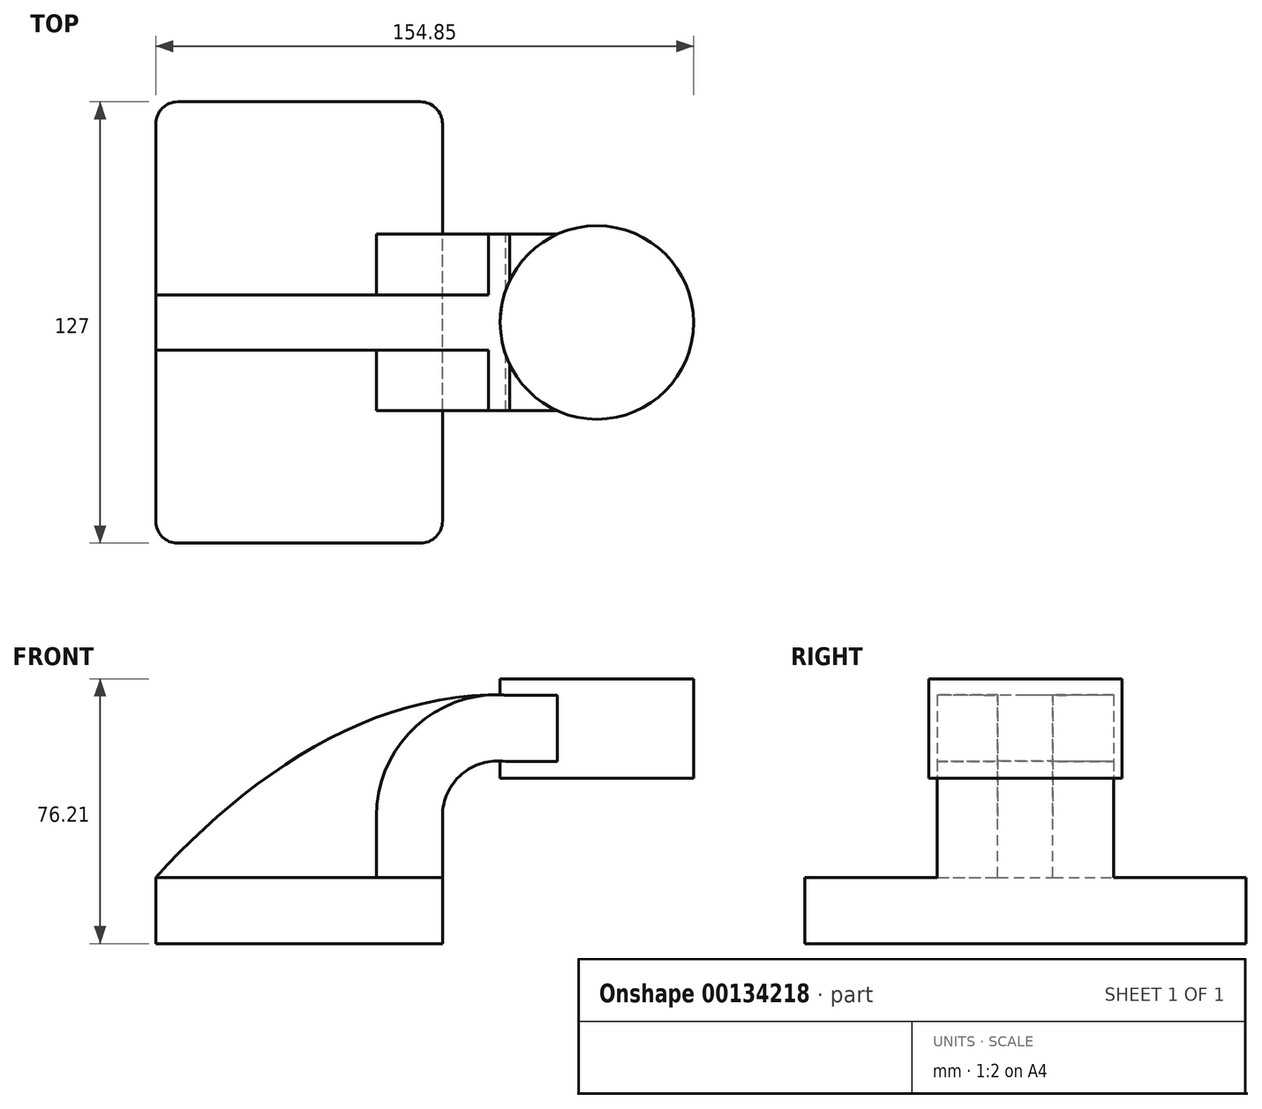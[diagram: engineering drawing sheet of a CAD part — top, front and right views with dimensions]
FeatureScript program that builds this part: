
annotation { "Feature Type Name" : "Feature", "Feature Type Description" : "" }
export const myFeature = defineFeature(function(context is Context, id is Id, definition is map)
    precondition{}
    {
        {
            var Q0;
            Q0=qCreatedBy(makeId("Front.planeOp"),FACE);
            var sketch = newSketch(context, id + "F0", { "sketchPlane" : qUnion([Q0])});
            skLineSegment(sketch, "E0.bottom", {"start": v(-41.28, 9.52) * mm, "end": v(41.27, 9.53) * mm});
            skLineSegment(sketch, "E0.top", {"start": v(-41.28, -9.52) * mm, "end": v(41.28, -9.52) * mm});
            skLineSegment(sketch, "E0.left", {"start": v(-41.28, 9.52) * mm, "end": v(-41.28, -9.53) * mm});
            skLineSegment(sketch, "E0.right", {"start": v(41.27, 9.53) * mm, "end": v(41.28, -9.52) * mm});
            skPoint(sketch, "E0.middle", {"position": v(0, 0) * mm});
            skLineSegment(sketch, "E1", {"start": v(41.27, 9.53) * mm, "end": v(41.27, 27.17) * mm});
            skLineSegment(sketch, "E2.bottom", {"start": v(62.77, 66.68) * mm, "end": v(113.57, 66.68) * mm});
            skLineSegment(sketch, "E2.top", {"start": v(62.77, 38.1) * mm, "end": v(113.57, 38.1) * mm});
            skLineSegment(sketch, "E2.left", {"start": v(62.77, 66.68) * mm, "end": v(62.77, 38.1) * mm});
            skLineSegment(sketch, "E2.right", {"start": v(113.57, 66.68) * mm, "end": v(113.57, 38.1) * mm});
            skArc(sketch, "E3", {"start": v(41.27, 27.17) * mm, "mid": v(46.77, 39.18) * mm, "end": v(59.46, 42.88) * mm});
            skLineSegment(sketch, "E4", {"start": v(59.46, 42.88) * mm, "end": v(85.72, 42.88) * mm});
            skLineSegment(sketch, "E5.0", {"start": v(60.58, 61.93) * mm, "end": v(85.72, 61.93) * mm});
            skArc(sketch, "E5.1", {"start": v(22.22, 27.17) * mm, "mid": v(33.7, 53.05) * mm, "end": v(60.58, 61.93) * mm});
            skLineSegment(sketch, "E5.2", {"start": v(22.22, 9.53) * mm, "end": v(22.22, 27.17) * mm});
            skLineSegment(sketch, "E6", {"start": v(85.72, 42.88) * mm, "end": v(85.72, 61.93) * mm});
            skFitSpline(sketch, "E7", {"points": [v(-41.28, 9.52) * mm, v(60.58, 61.93) * mm], "startDerivative": vector(80.3, 88.36) * mm, "endDerivative": vector(117.44, -5.38) * mm});
            skLineSegment(sketch, "E8", {"start": v(85.72, 61.93) * mm, "end": v(85.72, 38.1) * mm});
            skLineSegment(sketch, "E9", {"start": v(85.72, 38.1) * mm, "end": v(85.72, 66.68) * mm});
            skSolve(sketch);
        }
        {
            var Q0;
            Q0=makeQuery(id+"F0.imprint","IMPRINT",FACE,{"disambiguationData":[TD([[makeQuery(id+"F0.imprint","IMPRINT",EDGE,{"derivedFrom":sQuery(id+"F0.wireOp",EDGE,"E0.top")}),1.0]])]});
            extrude(context, id + "F1", {"entities" : qUnion([Q0]), "endBound" : BoundingType.SYMMETRIC, "depth" : 127 * mm});
        }
        {
            var Q0;
            {var subQ6=sQuery(id+"F0.wireOp",EDGE,"E1");Q0=makeQuery(id+"F0.imprint","IMPRINT",FACE,{"disambiguationData":[TD([[makeQuery(id+"F0.imprint","IMPRINT",EDGE,{"derivedFrom":subQ6}),1.0]])]});}
            var Q1;
            {var subQ0=sQuery(id+"F0.wireOp",EDGE,"E5.0");var subQ1=sQuery(id+"F0.wireOp",EDGE,"E2.left");var subQ2=makeQuery(id+"F0.imprint","INTERSECT",VERTEX,{"derivedFrom":[subQ1,subQ0]});Q1=makeQuery(id+"F0.imprint","IMPRINT",FACE,{"disambiguationData":[TD([[makeQuery(id+"F0.imprint","IMPRINT",EDGE,{"disambiguationData":[TD([[subQ2,-1.0]])],"derivedFrom":subQ1}),1.0]])]});}
            extrude(context, id + "F2", {"entities" : qUnion([Q0, Q1]), "operationType" : NewBodyOperationType.ADD, "endBound" : BoundingType.SYMMETRIC, "depth" : 50.8 * mm});
        }
        {
            var Q0;
            {var subQ3=sQuery(id+"F0.wireOp",EDGE,"E5.2");Q0=makeQuery(id+"F0.imprint","IMPRINT",FACE,{"disambiguationData":[TD([[makeQuery(id+"F0.imprint","IMPRINT",EDGE,{"derivedFrom":subQ3}),1.0]])]});}
            extrude(context, id + "F3", {"entities" : qUnion([Q0]), "operationType" : NewBodyOperationType.ADD, "endBound" : BoundingType.SYMMETRIC, "depth" : 15.88 * mm});
        }
        {
            var Q0;
            {var subQ0=sQuery(id+"F0.wireOp",EDGE,"E2.right");Q0=makeQuery(id+"F0.imprint","IMPRINT",FACE,{"disambiguationData":[TD([[makeQuery(id+"F0.imprint","IMPRINT",EDGE,{"derivedFrom":subQ0}),-1.0]])]});}
            var Q1;
            Q1=sQuery(id+"F0.wireOp",EDGE,"E9");
            revolve(context, id + "F4", {"operationType" : NewBodyOperationType.ADD, "entities" : qUnion([Q0]), "axis" : qUnion([Q1]), "revolveType" : RevolveType.FULL});
        }
        {
            var Q0;
            Q0=makeQuery(id+"F1.opExtrude","CAP_EDGE",EDGE,{"disambiguationData":[OSD([sQuery(id+"F0.wireOp",EDGE,"E0.right")])],"isStart":false});
            var Q1;
            Q1=makeQuery(id+"F1.opExtrude","CAP_EDGE",EDGE,{"disambiguationData":[OSD([sQuery(id+"F0.wireOp",EDGE,"E0.left")])],"isStart":false});
            var Q2;
            Q2=makeQuery(id+"F1.opExtrude","CAP_EDGE",EDGE,{"disambiguationData":[OSD([sQuery(id+"F0.wireOp",EDGE,"E0.right")])],"isStart":true});
            var Q3;
            Q3=makeQuery(id+"F1.opExtrude","CAP_EDGE",EDGE,{"disambiguationData":[OSD([sQuery(id+"F0.wireOp",EDGE,"E0.left")])],"isStart":true});
            fillet(context, id + "F5", {"entities" : qUnion([Q0, Q1, Q2, Q3]), "radius" : 6.35 * mm, "tangentPropagation" : true, "allowEdgeOverflow" : false});
        }
    });
